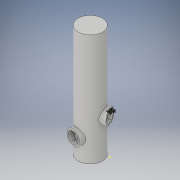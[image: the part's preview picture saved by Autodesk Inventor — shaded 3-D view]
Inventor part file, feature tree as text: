
AUTODESK INVENTOR PART (.ipt)
format: ipt  version: 2017 (Build 210142000, 142)  size: 1,444,864 bytes
history: native  units: in
note: dims shown in document units (in); Inventor stores cm internally (conversion verified against a paired STEP export)
features: extrude x27, sketch x22, other x17, loft x6, shell x1, plane x1
ambient origin geometry x8: Origin, YZ Plane, XZ Plane, XY Plane, X Axis, Y Axis, Z Axis, Center Point
bodies: Solid4 (feature_tree), Solid5 (feature_tree)
feature tree (74):
  shell  "shell and ramp"  Thickness=15.0in
  extrude  "outer cassing"  Depth=72.0in TaperAngle=0.0deg
  extrude  "bottom"  Depth=3.5in
  sketch  "Sketch2"  dims[d40=1.0in d41=0.0in d44=3.5in]
  other  "Work Axis1"
  other  "ramp"
  other  "ramp light"
  other  "top floor fill workplane"
  extrude  "top floor fill"  Depth=0.5in
  sketch  "Sketch5"  dims[d55=3.0in]
  other  "railing complete"
  other  "light ramp to complete"
  extrude  "top cap"  Depth=8.0in
  plane  "workplane sketch"
  other  "connection plane 1"
  other  "connection plane 2"
  other  "connection workplane 3"
  sketch  "Sketch19"  dims[d64=8.0in d65=1.0in d66=3.1201in d67=0.0in d68=90.0deg d69=90.0deg d70=0.0in d71=0.0in d146=9.0in]
  extrude  "bottom connection"  TaperAngle=90.0deg  [1 undecoded]
  extrude  "bottom connect to case"  TaperAngle=90.0deg  [1 undecoded]
  extrude  "connection cut"  Depth=1.0in TaperAngle=0.0deg
  extrude  "light bottom"  Depth=2.6875in TaperAngle=0.0deg
  sketch  "Sketch20"  dims[d147=1.1811in d149=360.0deg d151=90.0deg]
  extrude  "connetion 2"  Depth=1.0in TaperAngle=0.0deg
  extrude  "connection to case 2"  Depth=1.0in TaperAngle=0.0deg
  extrude  "connection cut 2"  Depth=20.15in
  extrude  "light 2"  Depth=1.0in TaperAngle=0.0deg
  loft  "connection ramp 2"
  sketch  "Sketch22"  dims[d152=90.0deg d153=90.0deg]
  extrude  "connection 3"  Depth=1.0in TaperAngle=0.0deg
  extrude  "connection to case 3"  Depth=52.15in
  extrude  "connection cut 3"  Depth=1.0in TaperAngle=0.0deg
  sketch  "Sketch38"  dims[d232=62.8in d233=1.0in d234=0.0in d237=1.0in d238=0.0in d239=0.0in d240=1.0in d241=0.0in d242=1.0in d243=0.0in d244=1.0in d245=0.0in d253=0.5833in d254=0.0625in d255=0.0625in d256=0.125in d257=2.0in d268=0.25in d269=0.125in d270=45.0deg d271=0.0892in d272=0.0884in d273=8.0in d274=1.0in d275=3.1201in d276=0.0in d277=90.0deg d278=90.0deg d279=0.0in d280=0.0in d308=3.0in d309=0.5in d310=3.0in d311=0.5833in d312=0.0625in d313=0.0625in d315=0.25in d316=0.125in d317=45.0deg d318=0.0892in d319=0.0884in d320=0.125in d321=90.0deg d322=90.0deg d323=0.0in d324=90.0deg d325=0.0in d326=90.0deg d327=1.0in d329=1.0in d330=0.0in d331=90.0deg d332=0.0in d333=90.0deg d335=1.0in d336=0.0in d337=90.0deg d338=0.0in d339=90.0deg d340=1.0in d341=0.0in d342=90.0deg d343=0.0in d344=90.0deg d346=1.0in d347=0.0in d348=90.0deg d349=0.0in d350=90.0deg d353=1.0in d354=0.0in d355=90.0deg d356=0.0in d357=90.0deg d367=0.5833in d368=0.0625in d369=0.0625in d370=0.25in d371=0.125in d372=0.0892in d373=0.0884in d374=0.125in d375=0.5833in d376=0.0625in d377=0.0625in d378=0.125in d379=1.0in d380=0.0in d381=0.5833in d382=0.0625in d383=0.0625in d384=0.125in d385=0.25in d386=0.125in d387=45.0deg d388=0.0892in d389=0.0884in d390=1.0in d391=0.0in d392=0.5833in d393=0.0625in d394=0.0625in d395=0.125in d396=0.25in d397=0.125in d398=45.0deg d399=0.0892in d400=0.0884in]
  loft  "connetion ramp 3"
  sketch  "Sketch23"  dims[d154=6.6667in d155=4.0in d156=1.0in d157=4.8944in d158=1.0in d159=0.0in]
  extrude  "connection 4"  Depth=0.0892in TaperAngle=0.0deg
  extrude  "connection to case 4"  Depth=0.0892in TaperAngle=0.0deg
  extrude  "connection cut 4"  TaperAngle=0.0deg  [1 undecoded]
  loft  "connection ramp 4"
  sketch  "Sketch24"  dims[d160=1.0in d161=0.0in d162=2.6875in d163=0.0in]
  extrude  "connection 5"  Depth=0.0892in TaperAngle=0.0deg
  extrude  "connection to case 5"  Depth=0.0892in TaperAngle=0.0deg
  extrude  "connection cut 5"  Depth=0.0892in
  loft  "connection ramp 5"
  sketch  "Sketch25"  dims[d164=9.48in]
  extrude  "connection 6"  TaperAngle=90.0deg  [1 undecoded]
  extrude  "connection to case 6"  TaperAngle=90.0deg  [1 undecoded]
  extrude  "connection cut 6"  TaperAngle=0.0deg  [1 undecoded]
  loft  "connection ramp 6"
  sketch  "Sketch26"  dims[d165=6.6667in d166=4.0in d167=1.0in d168=4.8944in d169=1.0in d170=0.0in d171=1.0in d172=0.0in]
  extrude  "connection 7"  Depth=0.0892in
  extrude  "connection to case 7"  Depth=0.0892in
  extrude  "connection cut 7"  TaperAngle=0.0deg  [1 undecoded]
  loft  "connection ramp 7"
  sketch  "Sketch1"  dims[d1=16.0in d2=72.0in d3=0.0in]
  sketch  "Sketch4"  dims[d53=3.0in d54=0.5in]
  sketch  "Sketch27"  dims[d173=2.625in d174=0.0in]
  sketch  "Sketch28"  dims[d178=6.6667in d179=4.0in d180=1.0in d181=4.8944in d182=1.0in d183=0.0in d184=1.0in d185=0.0in]
  other  "light railing"
  other  "light railing complete"
  sketch  "Sketch29"  dims[d186=1.0in d187=0.0in d188=20.15in]
  other  "Edges1"
  sketch  "Sketch30"  dims[d189=30.81in]
  other  "Edges2"
  sketch  "Sketch31"  dims[d190=6.6667in d191=4.0in d192=1.0in d193=4.8944in d194=1.0in d195=0.0in d196=1.0in d197=0.0in]
  other  "Edges3"
  sketch  "Sketch32"  dims[d198=1.0in d199=0.0in d200=41.48in]
  other  "Edges4"
  sketch  "Sketch33"  dims[d201=6.6667in d202=4.0in d203=1.0in d204=4.8944in d205=1.0in d206=0.0in d207=1.0in d208=0.0in]
  other  "Edges5"
  sketch  "Sketch35"  dims[d209=1.0in d210=0.0in d211=52.15in]
  other  "Edges6"
  sketch  "Sketch36"  dims[d213=6.6667in d214=4.0in d215=1.0in d216=4.8944in d217=1.0in d218=0.0in d219=1.0in d220=0.0in]
  sketch  "Sketch37"  dims[d221=1.0in d222=0.0in d228=6.6667in d229=4.0in d230=1.0in d231=4.8944in]
note: 7 required parameter values undecoded (feature->parameter linkage not recoverable at this tier; creation-order binding heuristic only, values carry confidence <= 0.55)
